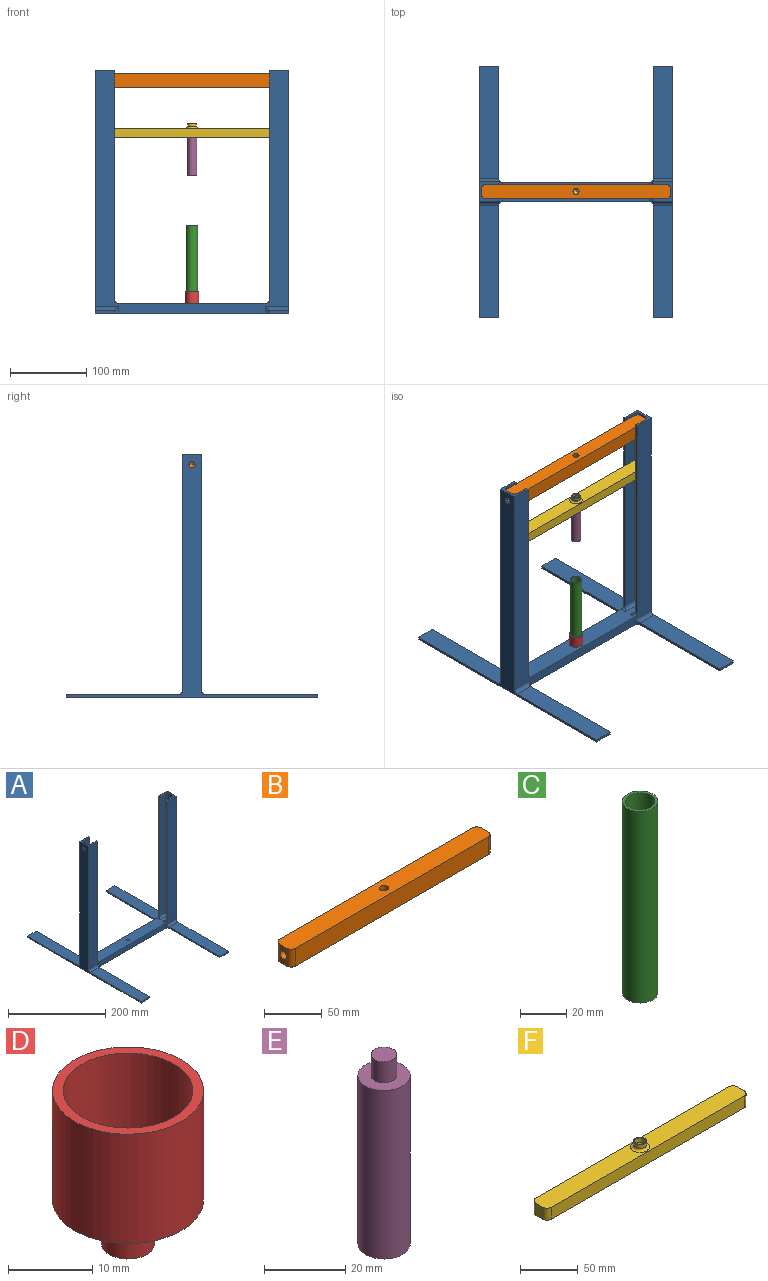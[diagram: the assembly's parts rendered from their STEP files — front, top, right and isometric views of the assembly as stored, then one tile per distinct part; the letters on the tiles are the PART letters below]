
ASSEMBLY  parts=6 mates=6
PART A: 60 faces, bbox 254x330.2x317.5 mm
  f0: plane 237.49x25.4mm, normal (0,0,1), area 5266.7mm2, adj f8,f14,f27,f40,f41,f42,f43,f44
  f1: plane 147.32x25.4mm, normal (0,0,1), area 3741.9mm2, adj f9,f10,f11,f25
  f2: plane 147.32x25.4mm, normal (0,0,1), area 3741.9mm2, adj f5,f6,f7,f19
  f3: plane 147.32x25.4mm, normal (0,0,1), area 3741.9mm2, adj f5,f15,f16,f23
  f4: plane 147.32x25.4mm, normal (0,0,1), area 3741.9mm2, adj f11,f12,f13,f21
  f5: plane 330.2x317.5mm, normal (-1,0,0), area 8993.8mm2, adj f2,f3,f6,f8,f14,f16,f17,f19
  f6: plane 25.4x3.18mm, normal (0,-1,0), area 80.6mm2, adj f2,f5,f7,f17
  f7: plane 147.32x3.18mm, normal (1,0,0), area 467.7mm2, adj f2,f6,f17,f18
  f8: plane 317.5x254mm, normal (0,-1,0), area 18217.5mm2, adj f0,f5,f11,f17,f18,f19,f24,f25
  f9: plane 147.32x3.18mm, normal (-1,0,0), area 467.7mm2, adj f1,f10,f17,f24
  f10: plane 25.4x3.18mm, normal (0,-1,0), area 80.6mm2, adj f1,f9,f11,f17
  f11: plane 330.2x317.5mm, normal (1,0,0), area 8993.8mm2, adj f1,f4,f8,f10,f12,f14,f17,f21
  f12: plane 25.4x3.18mm, normal (0,1,0), area 80.6mm2, adj f4,f11,f13,f17
  f13: plane 147.32x3.18mm, normal (-1,0,0), area 467.7mm2, adj f4,f12,f17,f20
  f14: plane 317.5x254mm, normal (0,1,0), area 18217.5mm2, adj f0,f5,f11,f17,f20,f21,f22,f23
  f15: plane 147.32x3.18mm, normal (1,0,0), area 467.7mm2, adj f3,f16,f17,f22
  f16: plane 25.4x3.18mm, normal (0,1,0), area 80.6mm2, adj f3,f5,f15,f17
  f17: plane 330.2x254mm, normal (0,0,-1), area 21957.6mm2, adj f5,f6,f7,f8,f9,f10,f11,f12
  f18: cylinder r=5.08mm len=8.26mm, axis (0,0,-1), area 40.1mm2, adj f7,f8,f17,f19
  f19: cylinder r=5.08mm len=30.48mm, axis (1,0,0), area 217.4mm2, adj f2,f5,f8,f18
  f20: cylinder r=5.08mm len=8.26mm, axis (0,0,-1), area 40.1mm2, adj f13,f14,f17,f21
  f21: cylinder r=5.08mm len=30.48mm, axis (-1,0,0), area 217.4mm2, adj f4,f11,f14,f20
  f22: cylinder r=5.08mm len=8.26mm, axis (0,0,-1), area 40.1mm2, adj f14,f15,f17,f23
  f23: cylinder r=5.08mm len=30.48mm, axis (-1,0,0), area 217.4mm2, adj f3,f5,f14,f22
  f24: cylinder r=5.08mm len=8.26mm, axis (0,0,-1), area 40.1mm2, adj f8,f9,f17,f25
  f25: cylinder r=5.08mm len=30.48mm, axis (1,0,0), area 217.4mm2, adj f1,f8,f11,f24
  f26: cone r=0mm half-angle=59deg, axis (0,0,1), area 36.9mm2, adj f27
  f27: cylinder r=3.17mm len=6.35mm, axis (0,0,1), area 126.7mm2, adj f0,f26
  f28: plane 299.72x3.18mm, normal (1,0,0), area 951.6mm2, adj f8,f29,f33,f40
  f29: plane 299.72x17.15mm, normal (0,1,0), area 5138.7mm2, adj f28,f33,f41,f50
  f30: plane 299.72x8.89mm, normal (1,0,0), area 2615mm2, adj f33,f42,f50,f52,f59
  f31: plane 299.72x17.15mm, normal (0,-1,0), area 5138.7mm2, adj f32,f33,f43,f52
  f32: plane 299.72x3.18mm, normal (1,0,0), area 951.6mm2, adj f14,f31,f33,f44
  f33: plane 25.4x25.4mm, normal (0,0,1), area 232.8mm2, adj f5,f8,f14,f28,f29,f30,f31,f32
  f34: plane 299.72x3.18mm, normal (-1,0,0), area 951.6mm2, adj f8,f38,f39,f45
  f35: plane 299.72x3.18mm, normal (-1,0,0), area 951.6mm2, adj f14,f36,f39,f49
  f36: plane 299.72x17.15mm, normal (0,-1,0), area 5138.7mm2, adj f35,f39,f48,f56
  f37: plane 299.72x8.89mm, normal (-1,0,0), area 2615mm2, adj f39,f47,f54,f56,f58
  f38: plane 299.72x17.15mm, normal (0,1,0), area 5138.7mm2, adj f34,f39,f46,f54
  f39: plane 25.4x25.4mm, normal (0,0,1), area 232.8mm2, adj f8,f11,f14,f34,f35,f36,f37,f38
  f40: cylinder r=5.08mm len=8.26mm, axis (0,1,0), area 40.1mm2, adj f0,f8,f28,f41
  f41: cylinder r=5.08mm len=22.23mm, axis (-1,0,0), area 151.5mm2, adj f0,f29,f40,f51
  f42: cylinder r=5.08mm len=8.89mm, axis (0,1,0), area 70.9mm2, adj f0,f30,f51,f53
  f43: cylinder r=5.08mm len=22.23mm, axis (1,0,0), area 151.5mm2, adj f0,f31,f44,f53
  f44: cylinder r=5.08mm len=8.26mm, axis (0,1,0), area 40.1mm2, adj f0,f14,f32,f43
  f45: cylinder r=5.08mm len=8.26mm, axis (0,-1,0), area 40.1mm2, adj f0,f8,f34,f46
  f46: cylinder r=5.08mm len=22.23mm, axis (-1,0,0), area 151.5mm2, adj f0,f38,f45,f55
  f47: cylinder r=5.08mm len=8.89mm, axis (0,-1,0), area 70.9mm2, adj f0,f37,f55,f57
  f48: cylinder r=5.08mm len=22.23mm, axis (1,0,0), area 151.5mm2, adj f0,f36,f49,f57
  f49: cylinder r=5.08mm len=8.26mm, axis (0,-1,0), area 40.1mm2, adj f0,f14,f35,f48
  f50: cylinder r=5.08mm len=299.72mm, axis (0,0,1), area 2391.7mm2, adj f29,f30,f33,f51
  f51: sphere r=5.08mm, area 40.5mm2, adj f41,f42,f50
  f52: cylinder r=5.08mm len=299.72mm, axis (0,0,1), area 2391.7mm2, adj f30,f31,f33,f53
  f53: sphere r=5.08mm, area 40.5mm2, adj f42,f43,f52
  f54: cylinder r=5.08mm len=299.72mm, axis (0,0,1), area 2391.7mm2, adj f37,f38,f39,f55
  f55: sphere r=5.08mm, area 40.5mm2, adj f46,f47,f54
  f56: cylinder r=5.08mm len=299.72mm, axis (0,0,1), area 2391.7mm2, adj f36,f37,f39,f57
  f57: sphere r=5.08mm, area 40.5mm2, adj f47,f48,f56
  f58: cylinder r=3.97mm len=7.94mm, axis (1,0,0), area 79.2mm2, adj f11,f37
  f59: cylinder r=3.97mm len=7.94mm, axis (-1,0,0), area 79.2mm2, adj f5,f30
PART B: 15 faces, bbox 247.7x19.1x19.1 mm
  f0: plane 237.49x19.05mm, normal (0,1,0), area 4524.2mm2, adj f4,f5,f6,f9
  f1: plane 19.05x8.89mm, normal (-1,0,0), area 119.9mm2, adj f4,f5,f6,f7,f13
  f2: plane 237.49x19.05mm, normal (0,-1,0), area 4524.2mm2, adj f4,f5,f7,f8
  f3: plane 19.05x8.89mm, normal (1,0,0), area 119.9mm2, adj f4,f5,f8,f9,f11
  f4: plane 247.65x19.05mm, normal (0,0,1), area 4646.1mm2, adj f0,f1,f2,f3,f6,f7,f8,f9
  f5: plane 247.65x19.05mm, normal (0,0,-1), area 4646.1mm2, adj f0,f1,f2,f3,f6,f7,f8,f9
  f6: cylinder r=5.08mm len=19.05mm, axis (0,0,-1), area 152mm2, adj f0,f1,f4,f5
  f7: cylinder r=5.08mm len=19.05mm, axis (0,0,-1), area 152mm2, adj f1,f2,f4,f5
  f8: cylinder r=5.08mm len=19.05mm, axis (0,0,-1), area 152mm2, adj f2,f3,f4,f5
  f9: cylinder r=5.08mm len=19.05mm, axis (0,0,-1), area 152mm2, adj f0,f3,f4,f5
  f10: cone r=0mm half-angle=59deg, axis (1,0,0), area 57.7mm2, adj f11
  f11: cylinder r=3.97mm len=50.8mm, axis (1,0,0), area 1266.8mm2, adj f3,f10
  f12: cone r=0mm half-angle=59deg, axis (-1,0,0), area 57.7mm2, adj f13
  f13: cylinder r=3.97mm len=50.8mm, axis (-1,0,0), area 1266.8mm2, adj f1,f12
  f14: cylinder r=3.97mm len=19.05mm, axis (0,0,1), area 475mm2, adj f4,f5
PART C: 4 faces, bbox 15.4x15.4x101.6 mm
  f0: cylinder r=7.7mm len=101.6mm, axis (0,0,-1), area 4913mm2, adj f1,f2
  f1: plane 15.39x15.39mm, normal (0,0,1), area 56.3mm2, adj f0,f3
  f2: plane 15.39x15.39mm, normal (0,0,-1), area 56.3mm2, adj f0,f3
  f3: cylinder r=6.43mm len=101.6mm, axis (0,0,1), area 4102.3mm2, adj f1,f2
PART D: 7 faces, bbox 17.9x17.9x22.2 mm
  f0: cylinder r=8.97mm len=17.93mm, axis (0,0,-1), area 894.3mm2, adj f1,f2
  f1: plane 17.93x17.93mm, normal (0,0,-1), area 220.9mm2, adj f0,f5
  f2: plane 17.93x17.93mm, normal (0,0,1), area 66.5mm2, adj f0,f3
  f3: cylinder r=7.7mm len=15.39mm, axis (0,0,-1), area 706.2mm2, adj f2,f4
  f4: plane 15.39x15.39mm, normal (0,0,1), area 186.1mm2, adj f3
  f5: cylinder r=3.17mm len=6.35mm, axis (0,0,1), area 126.7mm2, adj f1,f6
  f6: plane 6.35x6.35mm, normal (0,0,-1), area 31.7mm2, adj f5
PART E: 7 faces, bbox 12.9x12.9x57.2 mm
  f0: cylinder r=6.43mm len=50.8mm, axis (0,0,-1), area 2051.2mm2, adj f1,f2
  f1: plane 12.85x12.85mm, normal (0,0,1), area 98.1mm2, adj f0,f5
  f2: plane 12.85x12.85mm, normal (0,0,-1), area 83.8mm2, adj f0,f4
  f3: cone r=0mm half-angle=59deg, axis (0,0,-1), area 2.5mm2, adj f4
  f4: revolved ~7.65x7.65mm, area 91.2mm2, adj f2,f3
  f5: cylinder r=3.17mm len=6.35mm, axis (0,0,-1), area 126.7mm2, adj f1,f6
  f6: plane 6.35x6.35mm, normal (0,0,1), area 31.7mm2, adj f5
PART F: 18 faces, bbox 247.7x21.8x19.1 mm
  f0: plane 237.49x12.7mm, normal (0,1,0), area 3016.1mm2, adj f4,f5,f6,f9
  f1: plane 12.7x8.89mm, normal (-1,0,0), area 112.9mm2, adj f4,f5,f6,f7
  f2: plane 237.49x12.7mm, normal (0,-1,0), area 3016.1mm2, adj f4,f5,f7,f8
  f3: plane 12.7x8.89mm, normal (1,0,0), area 112.9mm2, adj f4,f5,f8,f9
  f4: plane 247.65x19.05mm, normal (0,0,1), area 4481.5mm2, adj f0,f1,f2,f3,f6,f7,f8,f9
  f5: plane 247.65x19.05mm, normal (0,0,-1), area 4663.9mm2, adj f0,f1,f2,f3,f6,f7,f8,f9
  f6: cylinder r=5.08mm len=12.7mm, axis (0,0,-1), area 101.3mm2, adj f0,f1,f4,f5
  f7: cylinder r=5.08mm len=12.7mm, axis (0,0,-1), area 101.3mm2, adj f1,f2,f4,f5
  f8: cylinder r=5.08mm len=12.7mm, axis (0,0,-1), area 101.3mm2, adj f2,f3,f4,f5
  f9: cylinder r=5.08mm len=12.7mm, axis (0,0,-1), area 101.3mm2, adj f0,f3,f4,f5
  f10: cone r=0mm half-angle=59deg, axis (0,0,-1), area 36.9mm2, adj f11
  f11: cylinder r=3.17mm len=6.35mm, axis (0,0,-1), area 126.7mm2, adj f5,f10
  f12: cylinder r=5.71mm len=11.43mm, axis (0,0,-1), area 136.8mm2, adj f13,f16
  f13: plane 11.43x11.43mm, normal (0,0,1), area 31.4mm2, adj f12,f15
  f14: cone r=0mm half-angle=59deg, axis (0,0,1), area 45.7mm2, adj f17
  f15: cylinder r=4.76mm len=9.53mm, axis (0,0,1), area 147mm2, adj f13,f17
  f16: torus R=8.26mm, axis (0,0,1), area 166.4mm2, adj f4,f12
  f17: torus R=2.22mm, axis (0,0,1), area 71.3mm2, adj f14,f15
PLACE A t=(-48.37,-318.09,43.95)mm
PLACE B t=(-48.37,-318.09,339.22)mm
PLACE C t=(-48.37,-318.09,56.96)mm
PLACE D t=(-48.37,-318.09,55.69)mm
PLACE E t=(-48.37,-318.09,224.06)mm
PLACE F t=(-48.37,-322.79,273.9)mm
MATE planar F.f1 <-> A.f30  axis (-1,0,0) through (-172.2,-318.09,280.25)mm
MATE revolute C.f0 <-> D.f0  axis (0,0,-1) through (-48.37,-318.09,56.96)mm
MATE revolute D.f5 <-> A.f26  axis (0,0,-1) through (-48.37,-318.09,49.34)mm
MATE revolute E.f5 <-> F.f10  axis (0,0,1) through (-48.37,-318.09,281.21)mm
MATE fastened B.f10 <-> A.f58  axis (1,0,0) through (75.45,-318.09,348.75)mm
MATE planar F.f2 <-> A.f29  axis (0,-1,0) through (-48.37,-327.62,280.25)mm
